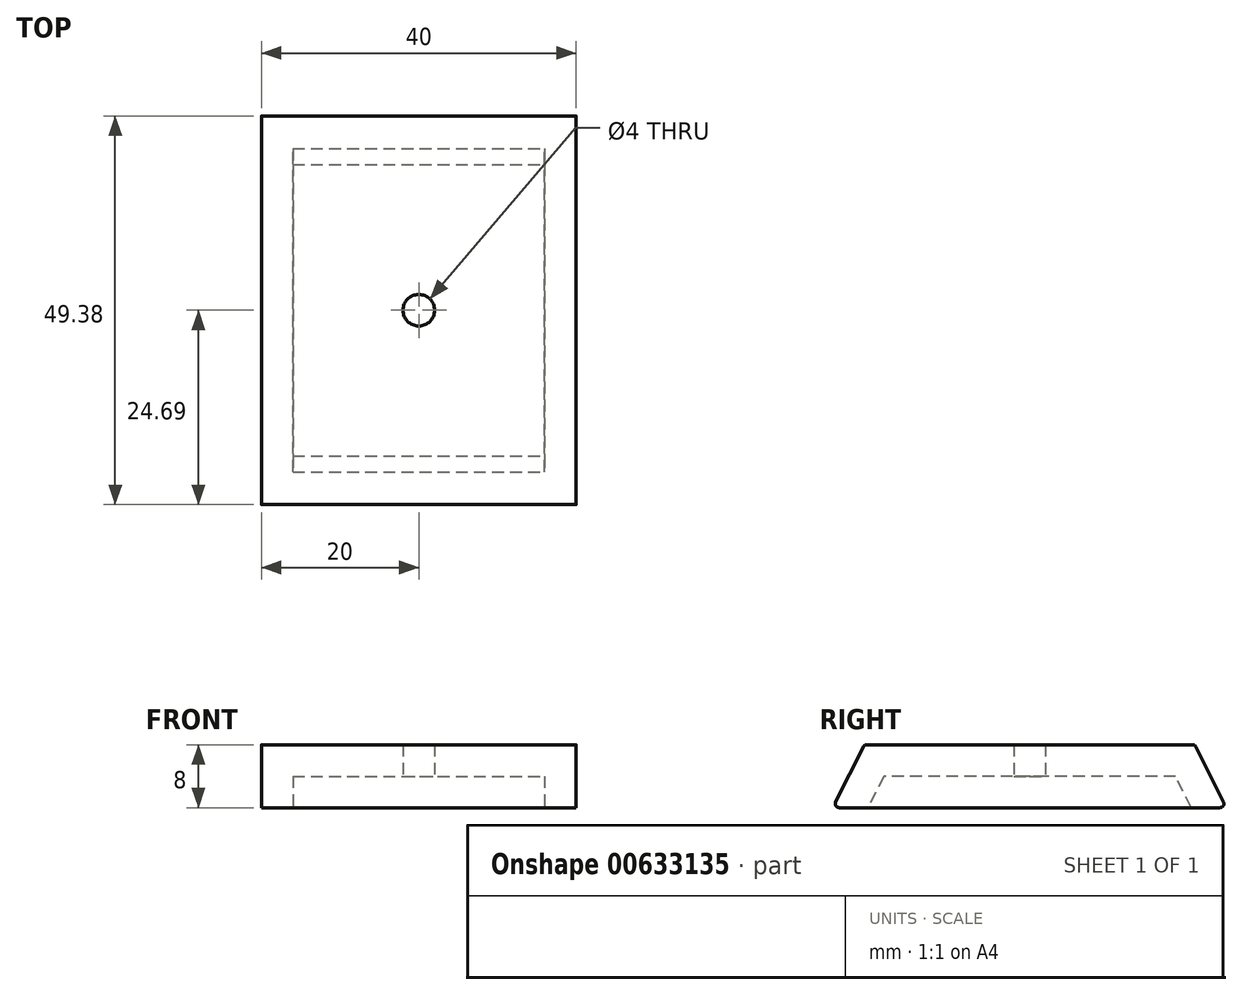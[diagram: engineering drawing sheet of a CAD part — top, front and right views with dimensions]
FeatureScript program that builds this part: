
annotation { "Feature Type Name" : "Feature", "Feature Type Description" : "" }
export const myFeature = defineFeature(function(context is Context, id is Id, definition is map)
    precondition{}
    {
        {
            var Q0;
            Q0=qCreatedBy(makeId("Right.planeOp"),FACE);
            var sketch = newSketch(context, id + "F0", { "sketchPlane" : qUnion([Q0])});
            skLineSegment(sketch, "E0", {"start": v(0, 0) * mm, "end": v(50, 0) * mm});
            skLineSegment(sketch, "E1", {"start": v(50, 0) * mm, "end": v(46, 8) * mm});
            skLineSegment(sketch, "E2", {"start": v(46, 8) * mm, "end": v(4, 8) * mm});
            skLineSegment(sketch, "E3", {"start": v(4, 8) * mm, "end": v(0, 0) * mm});
            skLineSegment(sketch, "E4", {"start": v(25, 0) * mm, "end": v(25, 8) * mm, "construction": true});
            skSolve(sketch);
        }
        {
            var Q0;
            Q0=makeQuery(id+"F0.imprint","IMPRINT",FACE,{"disambiguationData":[TD([[makeQuery(id+"F0.imprint","IMPRINT",EDGE,{"derivedFrom":sQuery(id+"F0.wireOp",EDGE,"E0")}),1.0]])]});
            extrude(context, id + "F1", {"entities" : qUnion([Q0]), "depth" : 40 * mm, "offsetDistance" : 25.4 * mm});
        }
        {
            var Q0;
            Q0=makeQuery(id+"F1.opExtrude","SWEPT_EDGE",EDGE,{"disambiguationData":[OSD([sQuery(id+"F0.wireOp",EDGE,"E2"),sQuery(id+"F0.wireOp",EDGE,"E3")])]});
            var Q1;
            Q1=makeQuery(id+"F1.opExtrude","SWEPT_EDGE",EDGE,{"disambiguationData":[OSD([sQuery(id+"F0.wireOp",EDGE,"E1"),sQuery(id+"F0.wireOp",EDGE,"E2")])]});
            var Q2;
            Q2=makeQuery(id+"F1.opExtrude","SWEPT_EDGE",EDGE,{"disambiguationData":[OSD([sQuery(id+"F0.wireOp",EDGE,"E0"),sQuery(id+"F0.wireOp",EDGE,"E3")])]});
            var Q3;
            Q3=makeQuery(id+"F1.opExtrude","SWEPT_EDGE",EDGE,{"disambiguationData":[OSD([sQuery(id+"F0.wireOp",EDGE,"E0"),sQuery(id+"F0.wireOp",EDGE,"E1")])]});
            fillet(context, id + "F2", {"entities" : qUnion([Q0, Q1, Q2, Q3]), "radius" : 0.5 * mm, "tangentPropagation" : true, "allowEdgeOverflow" : false});
        }
        {
            var Q0;
            Q0=makeQuery(id+"F1.opExtrude","SWEPT_FACE",FACE,{"disambiguationData":[OSD([sQuery(id+"F0.wireOp",EDGE,"E0")])]});
            shell(context, id + "F3", {"entities" : qUnion([Q0]), "thickness" : 4 * mm});
        }
        {
            var Q0;
            Q0=makeQuery(id+"F3.opShell","OFFSET_FACE",FACE,{"disambiguationData":[OSD([sQuery(id+"F0.wireOp",EDGE,"E2")])]});
            var sketch = newSketch(context, id + "F4", { "sketchPlane" : qUnion([Q0])});
            skCircle(sketch, "E5", {"center": v(20, -25) * mm, "radius": 2 * mm});
            skPoint(sketch, "E5.centerSnap0", {"position": v(36, -25) * mm});
            skPoint(sketch, "E5.centerSnap1", {"position": v(20, -43.53) * mm});
            skSolve(sketch);
        }
        {
            var Q0;
            Q0=makeQuery(id+"F4.imprint","IMPRINT",FACE,{"disambiguationData":[TD([[makeQuery(id+"F4.imprint","IMPRINT",EDGE,{"derivedFrom":sQuery(id+"F4.wireOp",EDGE,"E5")}),1.0]])]});
            var Q1;
            Q1=sQuery(id+"F4.wireOp",EDGE,"E5");
            var Q2;
            Q2=makeQuery(id+"F1.opExtrude","SWEPT_FACE",FACE,{"disambiguationData":[OSD([sQuery(id+"F0.wireOp",EDGE,"E2")])]});
            extrude(context, id + "F5", {"entities" : qUnion([Q0]), "operationType" : NewBodyOperationType.REMOVE, "surfaceEntities" : qUnion([Q1]), "endBound" : BoundingType.UP_TO_SURFACE, "oppositeDirection" : true, "depth" : 25 * mm, "endBoundEntityFace" : qUnion([Q2]), "offsetDistance" : 25 * mm});
        }
    });
